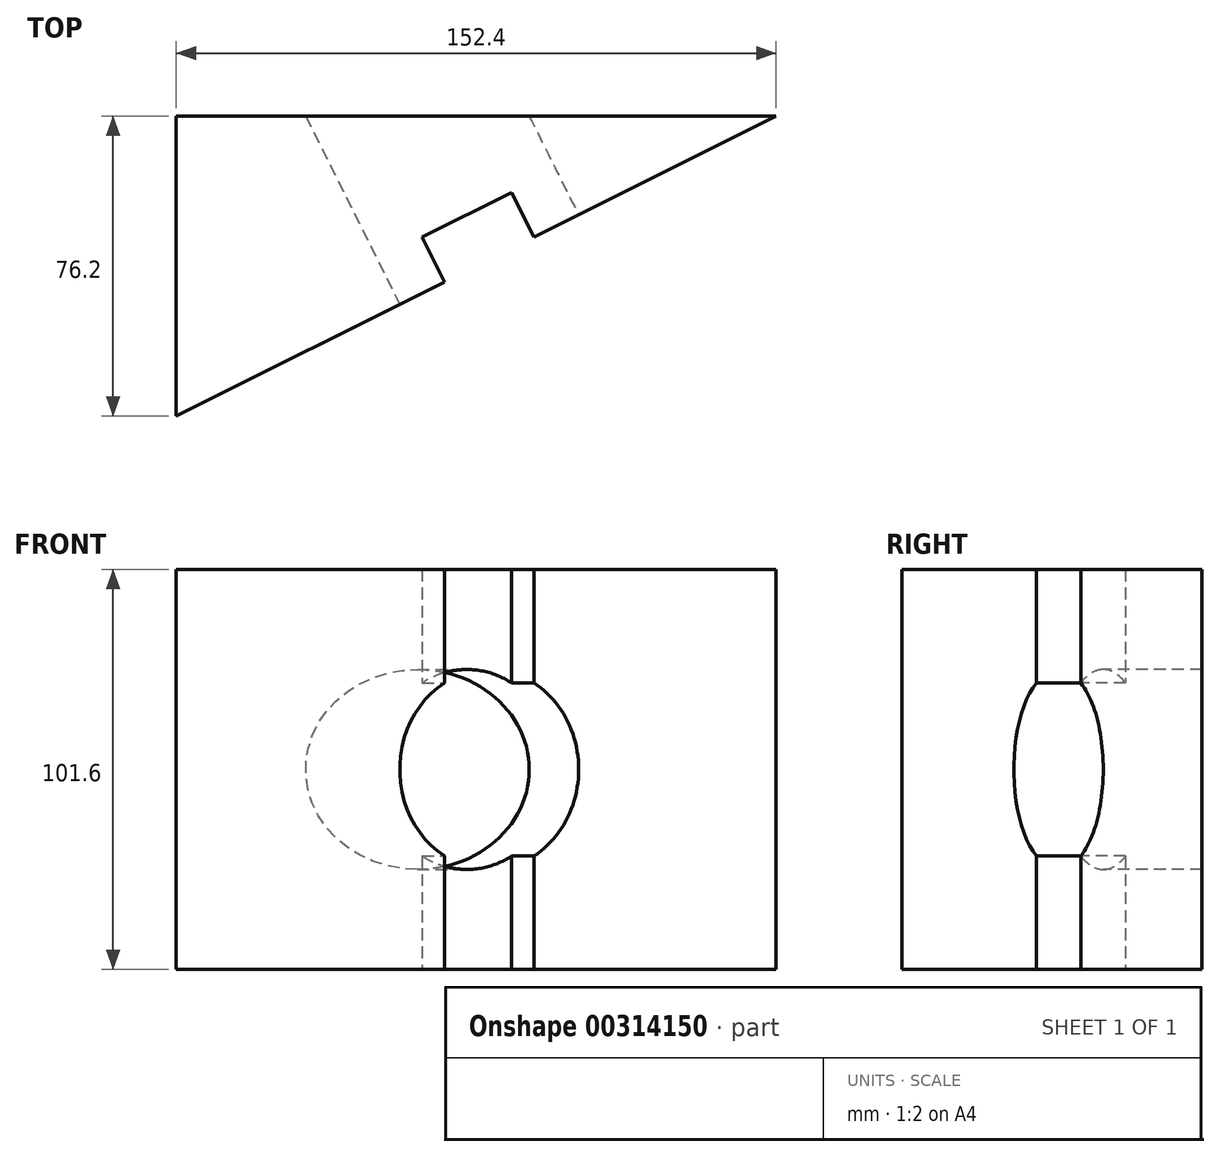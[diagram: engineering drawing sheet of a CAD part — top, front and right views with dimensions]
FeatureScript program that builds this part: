
annotation { "Feature Type Name" : "Feature", "Feature Type Description" : "" }
export const myFeature = defineFeature(function(context is Context, id is Id, definition is map)
    precondition{}
    {
        {
            var Q0;
            Q0=qCreatedBy(makeId("Top.planeOp"),FACE);
            var sketch = newSketch(context, id + "F0", { "sketchPlane" : qUnion([Q0])});
            skLineSegment(sketch, "E0.bottom", {"start": v(0, 0) * mm, "end": v(152.4, 0) * mm});
            skLineSegment(sketch, "E0.top", {"start": v(0, -76.2) * mm, "end": v(152.4, -76.2) * mm});
            skLineSegment(sketch, "E0.left", {"start": v(0, 0) * mm, "end": v(0, -76.2) * mm});
            skLineSegment(sketch, "E0.right", {"start": v(152.4, 0) * mm, "end": v(152.4, -76.2) * mm});
            skLineSegment(sketch, "E1", {"start": v(0, -76.2) * mm, "end": v(152.4, 0) * mm});
            skSolve(sketch);
        }
        {
            var Q0;
            Q0=makeQuery(id+"F0.imprint","IMPRINT",FACE,{"disambiguationData":[TD([[makeQuery(id+"F0.imprint","IMPRINT",EDGE,{"derivedFrom":sQuery(id+"F0.wireOp",EDGE,"E0.bottom")}),-1.0]])]});
            extrude(context, id + "F1", {"entities" : qUnion([Q0]), "depth" : 101.6 * mm});
        }
        {
            var Q0;
            Q0=makeQuery(id+"F1.opExtrude","SWEPT_FACE",FACE,{"disambiguationData":[OSD([sQuery(id+"F0.wireOp",EDGE,"E1")])]});
            var sketch = newSketch(context, id + "F2", { "sketchPlane" : qUnion([Q0])});
            skLineSegment(sketch, "E2.bottom", {"start": v(42.12, 101.6) * mm, "end": v(67.52, 101.6) * mm});
            skLineSegment(sketch, "E2.top", {"start": v(42.12, 0) * mm, "end": v(67.52, 0) * mm});
            skLineSegment(sketch, "E2.left", {"start": v(42.12, 101.6) * mm, "end": v(42.12, 0) * mm});
            skLineSegment(sketch, "E2.right", {"start": v(67.52, 101.6) * mm, "end": v(67.52, 0) * mm});
            skPoint(sketch, "E2.middle", {"position": v(54.82, 50.8) * mm});
            skSolve(sketch);
        }
        {
            var Q0;
            Q0=makeQuery(id+"F2.imprint","IMPRINT",FACE,{"disambiguationData":[TD([[makeQuery(id+"F2.imprint","IMPRINT",EDGE,{"derivedFrom":sQuery(id+"F2.wireOp",EDGE,"E2.bottom")}),-1.0]])]});
            extrude(context, id + "F3", {"entities" : qUnion([Q0]), "operationType" : NewBodyOperationType.REMOVE, "oppositeDirection" : true, "depth" : 12.7 * mm});
        }
        {
            var Q0;
            {var subQ0=sQuery(id+"F2.wireOp",EDGE,"E2.left");Q0=makeQuery(id+"F2.imprint","IMPRINT",FACE,{"disambiguationData":[TD([[makeQuery(id+"F2.imprint","IMPRINT",EDGE,{"derivedFrom":subQ0}),-1.0]])]});}
            var sketch = newSketch(context, id + "F4", { "sketchPlane" : qUnion([Q0])});
            skCircle(sketch, "E3", {"center": v(54.82, 50.8) * mm, "radius": 25.4 * mm});
            skSolve(sketch);
        }
        {
            var Q0;
            {var subQ0=sQuery(id+"F4.wireOp",EDGE,"E3");var subQ1=makeQuery(id+"F2.imprint","IMPRINT",EDGE,{"derivedFrom":sQuery(id+"F2.wireOp",EDGE,"E2.left")});var subQ2=makeQuery(id+"F4.imprint","INTERSECT",VERTEX,{"disambiguationData":[OD(0.0)],"derivedFrom":[subQ1,subQ0]});Q0=makeQuery(id+"F4.imprint","IMPRINT",FACE,{"disambiguationData":[TD([[makeQuery(id+"F4.imprint","IMPRINT",EDGE,{"disambiguationData":[TD([[subQ2,1.0]])],"derivedFrom":subQ0}),1.0]])]});}
            var Q1;
            {var subQ0=sQuery(id+"F4.wireOp",EDGE,"E3");var subQ1=makeQuery(id+"F2.imprint","IMPRINT",EDGE,{"derivedFrom":sQuery(id+"F2.wireOp",EDGE,"E2.left")});var subQ2=makeQuery(id+"F4.imprint","INTERSECT",VERTEX,{"disambiguationData":[OD(0.0)],"derivedFrom":[subQ1,subQ0]});Q1=makeQuery(id+"F4.imprint","IMPRINT",FACE,{"disambiguationData":[TD([[makeQuery(id+"F4.imprint","IMPRINT",EDGE,{"disambiguationData":[TD([[subQ2,-1.0]])],"derivedFrom":subQ0}),1.0]])]});}
            extrude(context, id + "F5", {"entities" : qUnion([Q0, Q1]), "operationType" : NewBodyOperationType.REMOVE, "endBound" : BoundingType.THROUGH_ALL, "oppositeDirection" : true, "depth" : 25.4 * mm});
        }
    });
